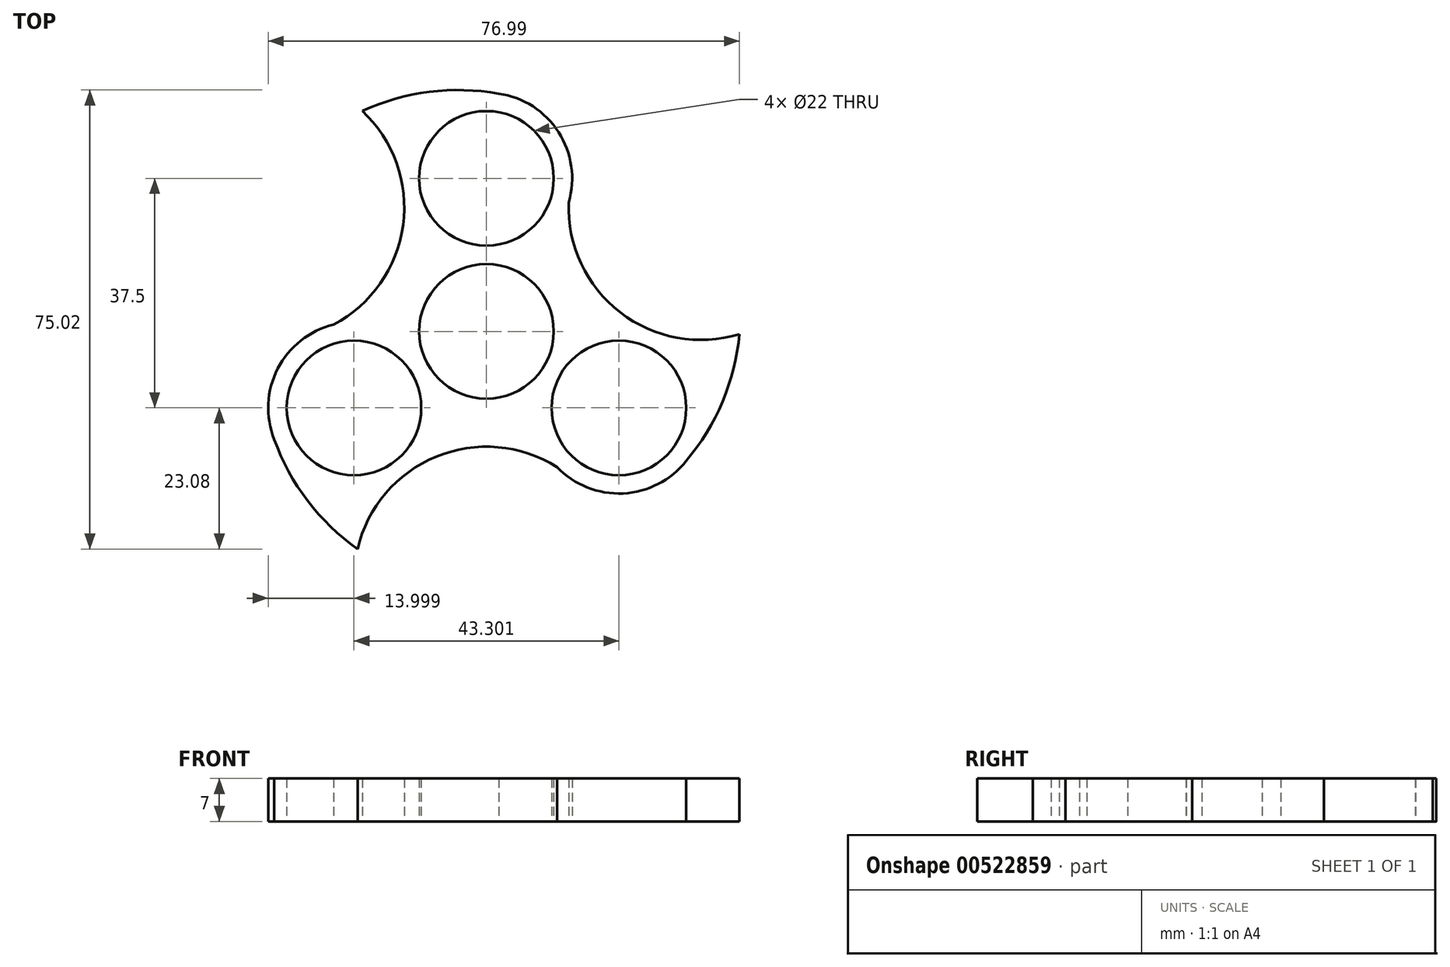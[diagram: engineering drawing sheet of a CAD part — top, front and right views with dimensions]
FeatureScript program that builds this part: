
annotation { "Feature Type Name" : "Feature", "Feature Type Description" : "" }
export const myFeature = defineFeature(function(context is Context, id is Id, definition is map)
    precondition{}
    {
        {
            var Q0;
            Q0=qCreatedBy(makeId("Top.planeOp"),FACE);
            var sketch = newSketch(context, id + "F0", { "sketchPlane" : qUnion([Q0])});
            skCircle(sketch, "E0", {"center": v(0, 25) * mm, "radius": 11 * mm});
            skCircle(sketch, "E1.1.0", {"center": v(-21.65, -12.5) * mm, "radius": 11 * mm});
            skCircle(sketch, "E1.2.0", {"center": v(21.65, -12.5) * mm, "radius": 11 * mm});
            skPoint(sketch, "E1.center", {"position": v(0, 0) * mm});
            skArc(sketch, "E2", {"start": v(-6.3, 12.5) * mm, "mid": v(-12.12, 7) * mm, "end": v(-13.98, -0.79) * mm});
            skArc(sketch, "E3", {"start": v(7.67, -11.71) * mm, "mid": v(33.77, -19.5) * mm, "end": v(13.98, -0.79) * mm});
            skArc(sketch, "E4.1.0", {"start": v(6.3, 12.5) * mm, "mid": v(0, 39) * mm, "end": v(-6.3, 12.5) * mm});
            skArc(sketch, "E4.2.0", {"start": v(-13.98, -0.79) * mm, "mid": v(-33.77, -19.5) * mm, "end": v(-7.67, -11.71) * mm});
            skArc(sketch, "E5.trimOffspring", {"start": v(13.98, -0.79) * mm, "mid": v(12.12, 7) * mm, "end": v(6.3, 12.5) * mm});
            skArc(sketch, "E6.trimOffspring", {"start": v(-7.67, -11.71) * mm, "mid": v(0, -14) * mm, "end": v(7.67, -11.71) * mm});
            skArc(sketch, "E7", {"start": v(-24.98, 1.1) * mm, "mid": v(-13.62, 17.35) * mm, "end": v(-20.28, 36.03) * mm});
            skArc(sketch, "E8", {"start": v(2.02, 38.85) * mm, "mid": v(-9.35, 39.14) * mm, "end": v(-20.28, 36.03) * mm});
            skArc(sketch, "E9.1.0", {"start": v(11.54, -22.18) * mm, "mid": v(-8.22, -20.47) * mm, "end": v(-21.06, -35.58) * mm});
            skArc(sketch, "E9.1.1", {"start": v(-34.66, -17.68) * mm, "mid": v(-29.22, -27.67) * mm, "end": v(-21.06, -35.58) * mm});
            skArc(sketch, "E9.2.0", {"start": v(13.44, 21.08) * mm, "mid": v(21.84, 3.12) * mm, "end": v(41.34, -0.45) * mm});
            skArc(sketch, "E9.2.1", {"start": v(32.64, -21.17) * mm, "mid": v(38.57, -11.47) * mm, "end": v(41.34, -0.45) * mm});
            skCircle(sketch, "E10", {"center": v(0, 0) * mm, "radius": 11 * mm});
            skSolve(sketch);
        }
        {
            var Q0;
            Q0=makeQuery(id+"F0.imprint","IMPRINT",FACE,{"disambiguationData":[TD([[makeQuery(id+"F0.imprint","IMPRINT",EDGE,{"derivedFrom":sQuery(id+"F0.wireOp",EDGE,"E0")}),-1.0]])]});
            var Q1;
            {var subQ0=sQuery(id+"F0.wireOp",EDGE,"E8");Q1=makeQuery(id+"F0.imprint","IMPRINT",FACE,{"disambiguationData":[TD([[makeQuery(id+"F0.imprint","IMPRINT",EDGE,{"derivedFrom":subQ0}),1.0]])]});}
            var Q2;
            {var subQ0=sQuery(id+"F0.wireOp",EDGE,"E9.2.1");Q2=makeQuery(id+"F0.imprint","IMPRINT",FACE,{"disambiguationData":[TD([[makeQuery(id+"F0.imprint","IMPRINT",EDGE,{"derivedFrom":subQ0}),1.0]])]});}
            var Q3;
            {var subQ0=sQuery(id+"F0.wireOp",EDGE,"E9.1.1");Q3=makeQuery(id+"F0.imprint","IMPRINT",FACE,{"disambiguationData":[TD([[makeQuery(id+"F0.imprint","IMPRINT",EDGE,{"derivedFrom":subQ0}),1.0]])]});}
            var Q4;
            {var subQ0=sQuery(id+"F0.wireOp",EDGE,"E2");Q4=makeQuery(id+"F0.imprint","IMPRINT",FACE,{"disambiguationData":[TD([[makeQuery(id+"F0.imprint","IMPRINT",EDGE,{"derivedFrom":subQ0}),-1.0]])]});}
            var Q5;
            {var subQ0=sQuery(id+"F0.wireOp",EDGE,"E5.trimOffspring");Q5=makeQuery(id+"F0.imprint","IMPRINT",FACE,{"disambiguationData":[TD([[makeQuery(id+"F0.imprint","IMPRINT",EDGE,{"derivedFrom":subQ0}),-1.0]])]});}
            var Q6;
            {var subQ0=sQuery(id+"F0.wireOp",EDGE,"E6.trimOffspring");Q6=makeQuery(id+"F0.imprint","IMPRINT",FACE,{"disambiguationData":[TD([[makeQuery(id+"F0.imprint","IMPRINT",EDGE,{"derivedFrom":subQ0}),-1.0]])]});}
            extrude(context, id + "F1", {"entities" : qUnion([Q0, Q1, Q2, Q3, Q4, Q5, Q6]), "depth" : 7 * mm, "offsetDistance" : 25 * mm});
        }
    });
